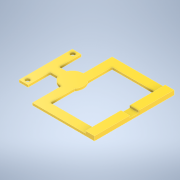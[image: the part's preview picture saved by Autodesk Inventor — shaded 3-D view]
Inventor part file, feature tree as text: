
AUTODESK INVENTOR PART (.ipt)
format: ipt  version: 2021 (Build 250183000, 183)  size: 172,544 bytes
history: native  units: mm
features: extrude x2, sketch x2, other x1, projected_geometry x1
ambient origin geometry x8: Origin, YZ Plane, XZ Plane, XY Plane, X Axis, Y Axis, Z Axis, Center Point
bodies: Solid1 (feature_tree)
feature tree (6):
  other  "<userpath>\Documents\Semestre8\Robótica\Proyecto-Rob\Piezas\ParámetrosGripper.xlsx"
  extrude  "Extrusion1"  Depth=20.0mm
  extrude  "Extrusion2"  Depth=200.0mm
  sketch  "Sketch1"  dims[d0=20.0mm d1=20.0mm]
  sketch  "Sketch2"  dims[d2=20.0mm d3=200.0mm d4=140.0mm d5=120.0mm d6=180.0mm d7=50.0mm d8=10.0mm d9=9.0mm d10=10.0mm d11=9.0mm d12=10.0mm d13=10.0mm d14=5.0mm d15=0.0mm d16=20.0mm d17=10.0mm d18=5.0mm d19=0.0mm]
  projected_geometry  "Projected Loop1"
